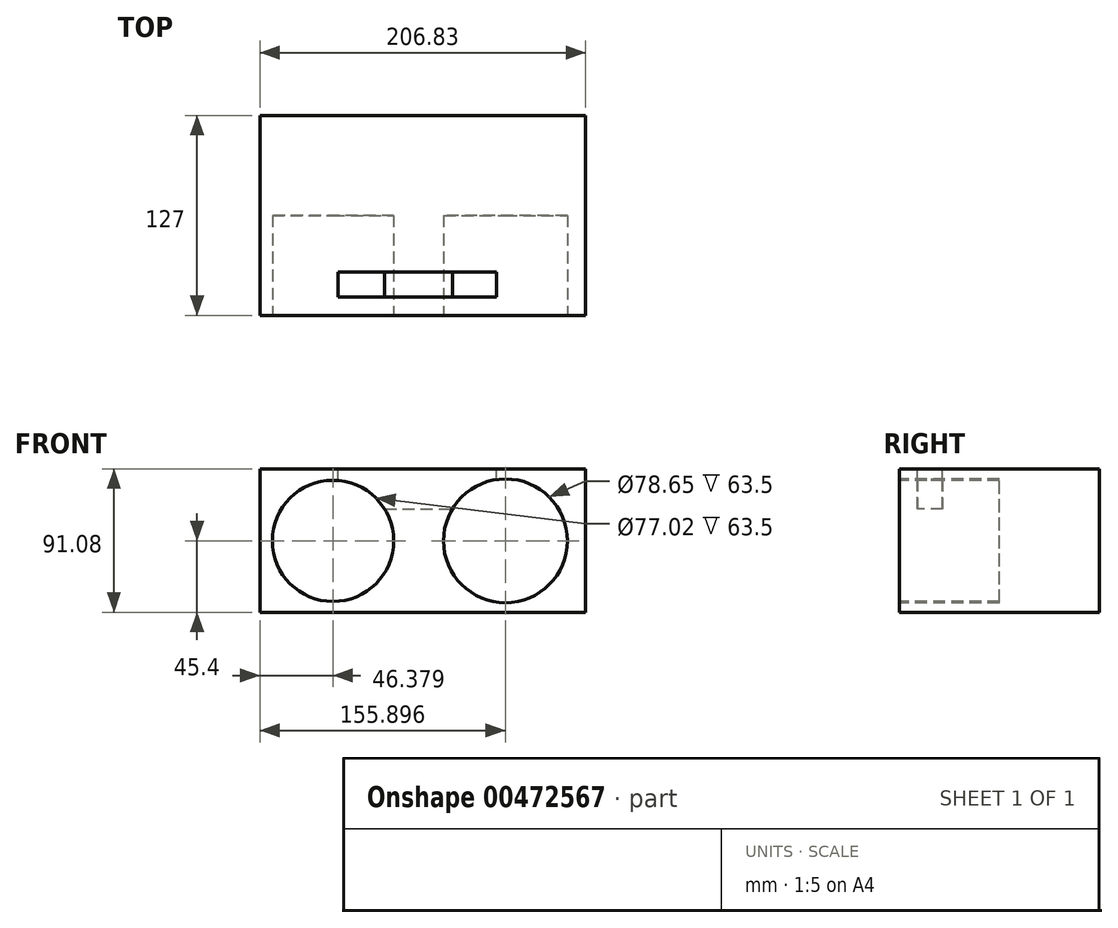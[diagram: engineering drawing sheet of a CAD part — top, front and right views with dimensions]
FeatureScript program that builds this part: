
annotation { "Feature Type Name" : "Feature", "Feature Type Description" : "" }
export const myFeature = defineFeature(function(context is Context, id is Id, definition is map)
    precondition{}
    {
        {
            var Q0;
            Q0=qCreatedBy(makeId("Front.planeOp"),FACE);
            var sketch = newSketch(context, id + "F0", { "sketchPlane" : qUnion([Q0])});
            skLineSegment(sketch, "E0.bottom", {"start": v(-61.7, 45.68) * mm, "end": v(145.12, 45.68) * mm});
            skLineSegment(sketch, "E0.top", {"start": v(-61.7, -45.4) * mm, "end": v(145.12, -45.4) * mm});
            skLineSegment(sketch, "E0.left", {"start": v(-61.7, 45.68) * mm, "end": v(-61.7, -45.4) * mm});
            skLineSegment(sketch, "E0.right", {"start": v(145.12, 45.68) * mm, "end": v(145.12, -45.4) * mm});
            skSolve(sketch);
        }
        {
            var Q0;
            Q0 = qSketchRegion(id + "F0", true);
            extrude(context, id + "F1", {"entities" : qUnion([Q0]), "depth" : 127 * mm});
        }
        {
            var Q0;
            Q0=makeQuery(id+"F0.imprint","IMPRINT",FACE,{"disambiguationData":[TD([[makeQuery(id+"F0.imprint","IMPRINT",EDGE,{"derivedFrom":sQuery(id+"F0.wireOp",EDGE,"E0.bottom")}),-1.0]])]});
            extrude(context, id + "F2", {"entities" : qUnion([Q0]), "operationType" : NewBodyOperationType.ADD, "depth" : 127 * mm});
        }
        {
            var Q0;
            Q0=makeQuery(id+"F1.opExtrude","CAP_FACE",FACE,{"disambiguationData":[OSD([sQuery(id+"F0.wireOp",EDGE,"E0.bottom"),sQuery(id+"F0.wireOp",EDGE,"E0.top"),sQuery(id+"F0.wireOp",EDGE,"E0.left"),sQuery(id+"F0.wireOp",EDGE,"E0.right")])],"isStart":false});
            var sketch = newSketch(context, id + "F3", { "sketchPlane" : qUnion([Q0])});
            skCircle(sketch, "E1", {"center": v(-15.33, 0) * mm, "radius": 38.5 * mm});
            skCircle(sketch, "E2", {"center": v(94.19, 0) * mm, "radius": 39.32 * mm});
            skSolve(sketch);
        }
        {
            var Q0;
            Q0=makeQuery(id+"F3.imprint","IMPRINT",FACE,{"disambiguationData":[TD([[makeQuery(id+"F3.imprint","IMPRINT",EDGE,{"derivedFrom":sQuery(id+"F3.wireOp",EDGE,"E1")}),1.0]])]});
            var Q1;
            Q1=makeQuery(id+"F3.imprint","IMPRINT",FACE,{"disambiguationData":[TD([[makeQuery(id+"F3.imprint","IMPRINT",EDGE,{"derivedFrom":sQuery(id+"F3.wireOp",EDGE,"E2")}),1.0]])]});
            extrude(context, id + "F4", {"entities" : qUnion([Q0, Q1]), "operationType" : NewBodyOperationType.REMOVE, "oppositeDirection" : true, "depth" : 63.5 * mm});
        }
        {
            var Q0;
            Q0=makeQuery(id+"F1.opExtrude","SWEPT_FACE",FACE,{"disambiguationData":[OSD([sQuery(id+"F0.wireOp",EDGE,"E0.bottom")])]});
            var sketch = newSketch(context, id + "F5", { "sketchPlane" : qUnion([Q0])});
            skLineSegment(sketch, "E3.bottom", {"start": v(-12.26, -99.55) * mm, "end": v(88.37, -99.55) * mm});
            skLineSegment(sketch, "E3.top", {"start": v(-12.26, -115.43) * mm, "end": v(88.37, -115.43) * mm});
            skLineSegment(sketch, "E3.left", {"start": v(-12.26, -99.55) * mm, "end": v(-12.26, -115.43) * mm});
            skLineSegment(sketch, "E3.right", {"start": v(88.37, -99.55) * mm, "end": v(88.37, -115.43) * mm});
            skSolve(sketch);
        }
        {
            var Q0;
            Q0 = qSketchRegion(id + "F5", true);
            extrude(context, id + "F6", {"entities" : qUnion([Q0]), "operationType" : NewBodyOperationType.REMOVE, "oppositeDirection" : true, "depth" : 25.4 * mm});
        }
    });
